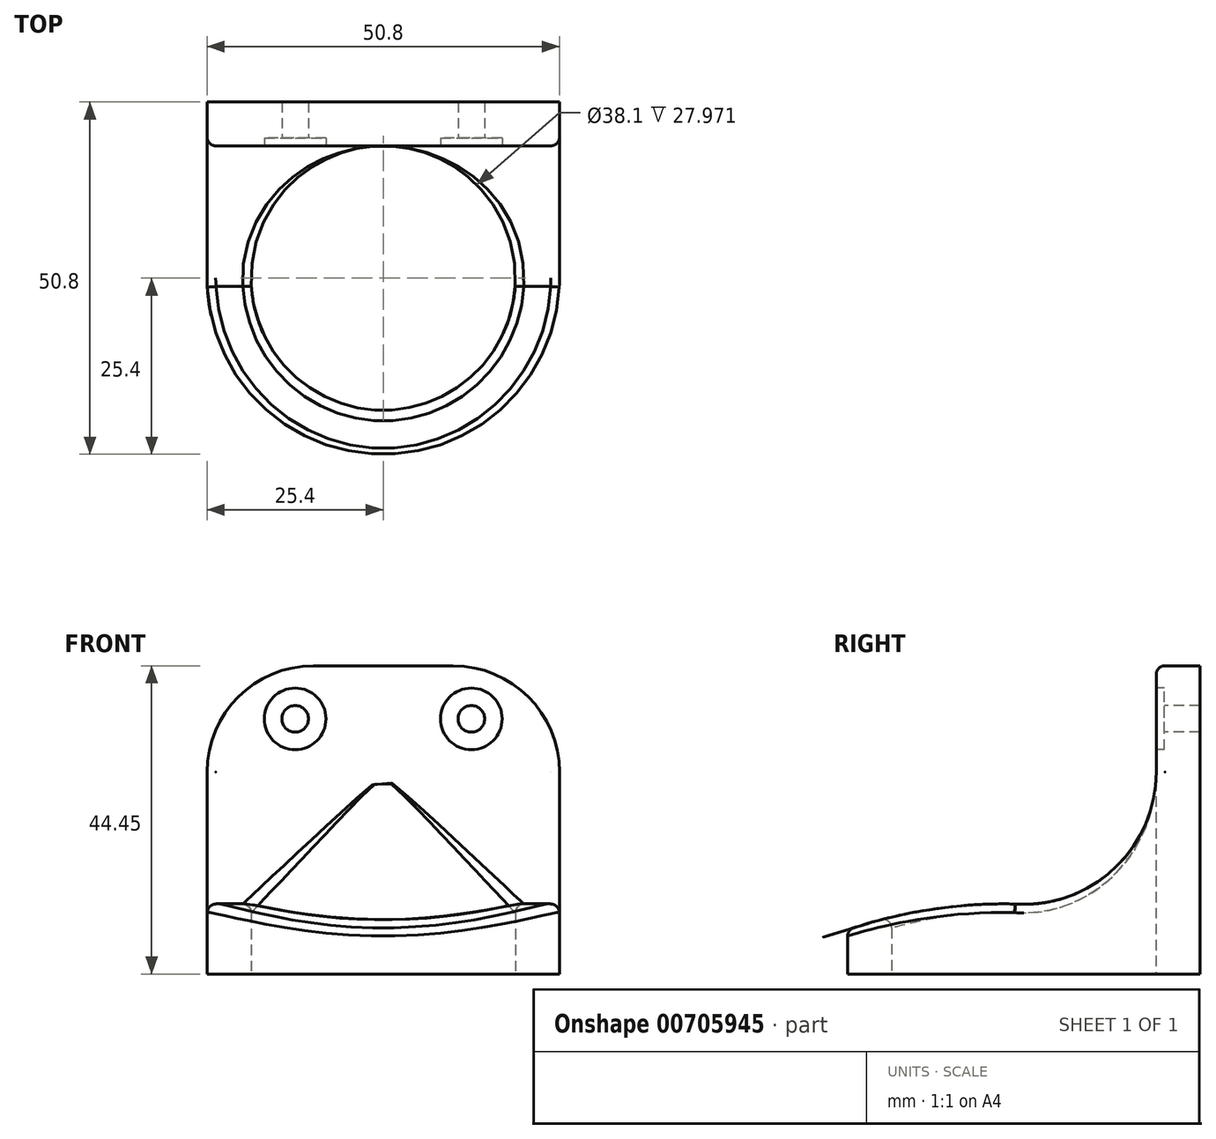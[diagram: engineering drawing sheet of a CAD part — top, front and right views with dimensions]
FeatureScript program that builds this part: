
annotation { "Feature Type Name" : "Feature", "Feature Type Description" : "" }
export const myFeature = defineFeature(function(context is Context, id is Id, definition is map)
    precondition{}
    {
        {
            var Q0;
            Q0=qCreatedBy(makeId("Top.planeOp"),FACE);
            var sketch = newSketch(context, id + "F0", { "sketchPlane" : qUnion([Q0])});
            skCircle(sketch, "E0", {"center": v(0, 0) * mm, "radius": 19.05 * mm});
            skArc(sketch, "E1", {"start": v(-25.4, 0) * mm, "mid": v(0, -25.4) * mm, "end": v(25.4, 0) * mm});
            skLineSegment(sketch, "E2.top", {"start": v(-25.4, 25.4) * mm, "end": v(0, 25.4) * mm});
            skLineSegment(sketch, "E2.left", {"start": v(-25.4, 0) * mm, "end": v(-25.4, 25.4) * mm});
            skLineSegment(sketch, "E3.MirrorCS", {"start": v(25.4, 0) * mm, "end": v(25.4, 25.4) * mm});
            skLineSegment(sketch, "E4.MirrorCS", {"start": v(25.4, 25.4) * mm, "end": v(0, 25.4) * mm});
            skSolve(sketch);
        }
        {
            var Q0;
            Q0 = qSketchRegion(id + "F0", true);
            extrude(context, id + "F1", {"entities" : qUnion([Q0]), "depth" : 6.35 * mm, "offsetDistance" : 25.4 * mm});
        }
        {
            var Q0;
            Q0=makeQuery(id+"F1.opExtrude","CAP_FACE",FACE,{"disambiguationData":[OSD([sQuery(id+"F0.wireOp",EDGE,"E0"),sQuery(id+"F0.wireOp",EDGE,"E1"),sQuery(id+"F0.wireOp",EDGE,"E2.top"),sQuery(id+"F0.wireOp",EDGE,"E2.left"),sQuery(id+"F0.wireOp",EDGE,"E3.MirrorCS"),sQuery(id+"F0.wireOp",EDGE,"E4.MirrorCS")])],"isStart":false});
            var sketch = newSketch(context, id + "F2", { "sketchPlane" : qUnion([Q0])});
            skCircle(sketch, "E5", {"center": v(0, 0) * mm, "radius": 19.05 * mm});
            skArc(sketch, "E6", {"start": v(-25.4, 0) * mm, "mid": v(0, -25.4) * mm, "end": v(25.4, 0) * mm});
            skLineSegment(sketch, "E7.top", {"start": v(-25.4, 25.4) * mm, "end": v(0, 25.4) * mm});
            skLineSegment(sketch, "E7.left", {"start": v(-25.4, 0) * mm, "end": v(-25.4, 25.4) * mm});
            skLineSegment(sketch, "E8.MirrorCS", {"start": v(25.4, 0) * mm, "end": v(25.4, 25.4) * mm});
            skLineSegment(sketch, "E9.MirrorCS", {"start": v(25.4, 25.4) * mm, "end": v(0, 25.4) * mm});
            skSolve(sketch);
        }
        {
            var Q0;
            Q0 = qSketchRegion(id + "F2", true);
            extrude(context, id + "F3", {"entities" : qUnion([Q0]), "operationType" : NewBodyOperationType.ADD, "depth" : 38.1 * mm, "offsetDistance" : 25.4 * mm});
        }
        {
            var Q0;
            Q0=qCreatedBy(makeId("Right.planeOp"),FACE);
            var sketch = newSketch(context, id + "F4", { "sketchPlane" : qUnion([Q0])});
            skArc(sketch, "E10", {"start": v(-1.2, 10.1) * mm, "mid": v(13.06, 15.22) * mm, "end": v(19.09, 29.14) * mm});
            skArc(sketch, "E11", {"start": v(0, 10.05) * mm, "mid": v(-12.88, 9.38) * mm, "end": v(-25.41, 6.37) * mm});
            skLineSegment(sketch, "E12", {"start": v(19.09, 6.37) * mm, "end": v(12.67, 6.37) * mm});
            skLineSegment(sketch, "E13", {"start": v(19.09, 29.14) * mm, "end": v(19.09, 45.44) * mm});
            skLineSegment(sketch, "E14", {"start": v(19.09, 45.44) * mm, "end": v(-26.2, 45.44) * mm});
            skLineSegment(sketch, "E15", {"start": v(-26.2, 45.44) * mm, "end": v(-26.2, 6.37) * mm});
            skLineSegment(sketch, "E16", {"start": v(-26.2, 6.37) * mm, "end": v(-25.41, 6.37) * mm});
            skSolve(sketch);
        }
        {
            var Q0;
            Q0 = qSketchRegion(id + "F4", true);
            extrude(context, id + "F5", {"entities" : qUnion([Q0]), "operationType" : NewBodyOperationType.REMOVE, "endBound" : BoundingType.SYMMETRIC, "oppositeDirection" : true, "depth" : 68.58 * mm, "offsetDistance" : 25.4 * mm});
        }
        {
            var Q0;
            Q0=makeQuery(id+"F3.opExtrude","CAP_EDGE",EDGE,{"disambiguationData":[OSD([sQuery(id+"F2.wireOp",EDGE,"E7.left")])],"isStart":false});
            var Q1;
            Q1=makeQuery(id+"F3.opExtrude","CAP_EDGE",EDGE,{"disambiguationData":[OSD([sQuery(id+"F2.wireOp",EDGE,"E8.MirrorCS")])],"isStart":false});
            fillet(context, id + "F6", {"entities" : qUnion([Q0, Q1]), "radius" : 15.33 * mm, "tangentPropagation" : true, "allowEdgeOverflow" : false});
        }
        {
            var Q0;
            Q0=makeQuery(id+"F5.boolean.opBoolean","COPY",FACE,{"derivedFrom":makeQuery(id+"F5.opExtrude","SWEPT_FACE",FACE,{"disambiguationData":[OSD([sQuery(id+"F4.wireOp",EDGE,"E13")])]})});
            var sketch = newSketch(context, id + "F7", { "sketchPlane" : qUnion([Q0])});
            skPoint(sketch, "E17.endSnap0", {"position": v(0, 36.8) * mm});
            skCircle(sketch, "E18", {"center": v(-12.7, 36.8) * mm, "radius": 4.44 * mm});
            skCircle(sketch, "E19", {"center": v(-12.7, 36.8) * mm, "radius": 1.92 * mm});
            skCircle(sketch, "E20.MirrorC", {"center": v(12.7, 36.8) * mm, "radius": 4.44 * mm});
            skCircle(sketch, "E21.MirrorC", {"center": v(12.7, 36.8) * mm, "radius": 1.92 * mm});
            skPoint(sketch, "E17.start.orphan", {"position": v(-12.7, 29.14) * mm});
            skPoint(sketch, "E22.orphan", {"position": v(-25.4, 29.14) * mm});
            skPoint(sketch, "E23.orphan", {"position": v(0, 29.14) * mm});
            skPoint(sketch, "E24.end.orphan", {"position": v(0, 44.45) * mm});
            skSolve(sketch);
        }
        {
            var Q0;
            Q0 = qSketchRegion(id + "F7", true);
            extrude(context, id + "F8", {"entities" : qUnion([Q0]), "operationType" : NewBodyOperationType.REMOVE, "oppositeDirection" : true, "depth" : 1.14 * mm, "offsetDistance" : 25.4 * mm});
        }
        {
            var Q0;
            Q0=makeQuery(id+"F8.boolean.opBoolean","SPLIT",FACE,{"disambiguationData":[TD([makeQuery(id+"F8.opExtrude","SWEPT_FACE",FACE,{"disambiguationData":[OSD([sQuery(id+"F7.wireOp",EDGE,"E19")])]})])],"derivedFrom":makeQuery(id+"F5.boolean.opBoolean","COPY",FACE,{"derivedFrom":makeQuery(id+"F5.opExtrude","SWEPT_FACE",FACE,{"disambiguationData":[OSD([sQuery(id+"F4.wireOp",EDGE,"E13")])]})})});
            var Q1;
            Q1=makeQuery(id+"F8.boolean.opBoolean","SPLIT",FACE,{"disambiguationData":[TD([makeQuery(id+"F8.opExtrude","SWEPT_FACE",FACE,{"disambiguationData":[OSD([sQuery(id+"F7.wireOp",EDGE,"E21.MirrorC")])]})])],"derivedFrom":makeQuery(id+"F5.boolean.opBoolean","COPY",FACE,{"derivedFrom":makeQuery(id+"F5.opExtrude","SWEPT_FACE",FACE,{"disambiguationData":[OSD([sQuery(id+"F4.wireOp",EDGE,"E13")])]})})});
            extrude(context, id + "F9", {"entities" : qUnion([Q0, Q1]), "operationType" : NewBodyOperationType.REMOVE, "oppositeDirection" : true, "depth" : 25.4 * mm, "offsetDistance" : 25.4 * mm});
        }
        {
            var Q0;
            Q0=makeQuery(id+"F5.boolean.opBoolean","INTERSECT",EDGE,{"derivedFrom":[makeQuery(id+"F3.boolean.opBoolean","MERGE",FACE,{"derivedFrom":[makeQuery(id+"F1.opExtrude","SWEPT_FACE",FACE,{"disambiguationData":[OSD([sQuery(id+"F0.wireOp",EDGE,"E0")])]}),makeQuery(id+"F3.opExtrude","SWEPT_FACE",FACE,{"disambiguationData":[OSD([sQuery(id+"F2.wireOp",EDGE,"E5")])]})]}),makeQuery(id+"F5.opExtrude","SWEPT_FACE",FACE,{"disambiguationData":[OSD([sQuery(id+"F4.wireOp",EDGE,"E10")])]})]});
            var Q1;
            Q1=makeQuery(id+"F5.boolean.opBoolean","INTERSECT",EDGE,{"derivedFrom":[makeQuery(id+"F3.boolean.opBoolean","MERGE",FACE,{"derivedFrom":[makeQuery(id+"F1.opExtrude","SWEPT_FACE",FACE,{"disambiguationData":[OSD([sQuery(id+"F0.wireOp",EDGE,"E0")])]}),makeQuery(id+"F3.opExtrude","SWEPT_FACE",FACE,{"disambiguationData":[OSD([sQuery(id+"F2.wireOp",EDGE,"E5")])]})]}),makeQuery(id+"F5.opExtrude","SWEPT_FACE",FACE,{"disambiguationData":[OSD([sQuery(id+"F4.wireOp",EDGE,"E11")])]})]});
            fillet(context, id + "F10", {"entities" : qUnion([Q0, Q1]), "radius" : 1.24 * mm, "tangentPropagation" : true, "allowEdgeOverflow" : false});
        }
        {
            var Q0;
            Q0=makeQuery(id+"F5.boolean.opBoolean","INTERSECT",EDGE,{"derivedFrom":[makeQuery(id+"F3.boolean.opBoolean","MERGE",FACE,{"derivedFrom":[makeQuery(id+"F1.opExtrude","SWEPT_FACE",FACE,{"disambiguationData":[OSD([sQuery(id+"F0.wireOp",EDGE,"E1")])]}),makeQuery(id+"F3.opExtrude","SWEPT_FACE",FACE,{"disambiguationData":[OSD([sQuery(id+"F2.wireOp",EDGE,"E6")])]})]}),makeQuery(id+"F5.opExtrude","SWEPT_FACE",FACE,{"disambiguationData":[OSD([sQuery(id+"F4.wireOp",EDGE,"E11")])]})]});
            var Q1;
            Q1=makeQuery(id+"F5.boolean.opBoolean","INTERSECT",EDGE,{"derivedFrom":[makeQuery(id+"F3.boolean.opBoolean","MERGE",FACE,{"derivedFrom":[makeQuery(id+"F1.opExtrude","SWEPT_FACE",FACE,{"disambiguationData":[OSD([sQuery(id+"F0.wireOp",EDGE,"E3.MirrorCS")])]}),makeQuery(id+"F3.opExtrude","SWEPT_FACE",FACE,{"disambiguationData":[OSD([sQuery(id+"F2.wireOp",EDGE,"E8.MirrorCS")])]})]}),makeQuery(id+"F5.opExtrude","SWEPT_FACE",FACE,{"disambiguationData":[OSD([sQuery(id+"F4.wireOp",EDGE,"E10")])]})]});
            var Q2;
            Q2=makeQuery(id+"F5.boolean.opBoolean","INTERSECT",EDGE,{"derivedFrom":[makeQuery(id+"F3.boolean.opBoolean","MERGE",FACE,{"derivedFrom":[makeQuery(id+"F1.opExtrude","SWEPT_FACE",FACE,{"disambiguationData":[OSD([sQuery(id+"F0.wireOp",EDGE,"E2.left")])]}),makeQuery(id+"F3.opExtrude","SWEPT_FACE",FACE,{"disambiguationData":[OSD([sQuery(id+"F2.wireOp",EDGE,"E7.left")])]})]}),makeQuery(id+"F5.opExtrude","SWEPT_FACE",FACE,{"disambiguationData":[OSD([sQuery(id+"F4.wireOp",EDGE,"E10")])]})]});
            fillet(context, id + "F11", {"entities" : qUnion([Q0, Q1, Q2]), "radius" : 1.24 * mm, "tangentPropagation" : true, "allowEdgeOverflow" : false});
        }
    });
